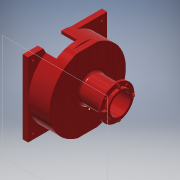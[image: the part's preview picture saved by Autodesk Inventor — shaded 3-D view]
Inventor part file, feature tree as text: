
AUTODESK INVENTOR PART (.ipt)
format: ipt  version: 2019 (Build 230136000, 136)  size: 973,824 bytes
history: native  units: mm
features: sketch x42, extrude x40, projected_geometry x19, other x6, fillet x6, reference x2
ambient origin geometry x8: Origin, YZ Plane, XZ Plane, XY Plane, X Axis, Y Axis, Z Axis, Center Point
bodies: Body1 (feature_tree), Body2 (feature_tree)
feature tree (115):
  other  "Твердое тело1"
  other  "0ae4c1a17e304db4a8c8e39318f74883.stl"
  extrude  "Выдавливание1"  Depth=3.0mm TaperAngle=0.0deg
  extrude  "Выдавливание2"  Depth=43.0mm
  extrude  "Выдавливание3"  Depth=25.0mm TaperAngle=0.0deg
  extrude  "Выдавливание4"  Depth=20.0mm
  extrude  "Выдавливание5"  Depth=20.0mm
  extrude  "Выдавливание6"  Depth=50.0mm TaperAngle=0.0deg
  extrude  "Выдавливание7"  Depth=34.0mm
  extrude  "Выдавливание8"  Depth=2.0mm
  extrude  "Выдавливание9"  Depth=2.0mm
  extrude  "Выдавливание10"  Depth=1.0mm TaperAngle=0.0deg
  sketch  "Эскиз15"
  sketch  "Эскиз16"
  extrude  "Выдавливание11"  Depth=25.0mm TaperAngle=0.0deg
  extrude  "Выдавливание12"  Depth=4.0mm
  extrude  "Выдавливание13"  Depth=4.0mm
  extrude  "Выдавливание14"  Depth=4.0mm
  extrude  "Выдавливание15"  Depth=4.0mm
  extrude  "Выдавливание16"  Depth=4.5mm
  fillet  "Сопряжение1"  Radius=4.5mm
  fillet  "Сопряжение2"  Radius=4.5mm
  extrude  "Выдавливание17"  Depth=4.5mm
  extrude  "Выдавливание18"  Depth=25.0mm TaperAngle=0.0deg
  extrude  "Выдавливание19"  Depth=7.2mm
  extrude  "Выдавливание20"  Depth=7.2mm
  extrude  "Выдавливание21"  Depth=7.2mm
  extrude  "Выдавливание22"  Depth=7.2mm
  fillet  "Сопряжение3"  Radius=2.0mm
  extrude  "Выдавливание23"  Depth=15.0mm TaperAngle=0.0deg
  extrude  "Выдавливание24"  Depth=15.0mm
  extrude  "Выдавливание25"  Depth=3.0mm
  extrude  "Выдавливание26"  Depth=13.663525mm
  extrude  "Выдавливание27"  Depth=30.32705mm
  extrude  "Выдавливание28"  Depth=8.5mm TaperAngle=0.0deg
  fillet  "Сопряжение4"  Radius=8.5mm
  extrude  "Выдавливание29"  Depth=38.8mm
  extrude  "Выдавливание30"  Depth=22.0mm TaperAngle=0.0deg
  extrude  "Выдавливание31"  Depth=25.0mm TaperAngle=0.0deg
  extrude  "Выдавливание32"  Depth=10.0mm TaperAngle=0.0deg
  fillet  "Сопряжение5"  Radius=3.5mm
  sketch  "Эскиз38"
  extrude  "Выдавливание33"  Depth=3.5mm TaperAngle=0.0deg
  extrude  "Выдавливание34"  Depth=1.0mm TaperAngle=0.0deg
  extrude  "Выдавливание35"  Depth=2.0mm
  fillet  "Сопряжение6"  Radius=2.0mm
  extrude  "Выдавливание37"  Depth=10.0mm TaperAngle=0.0deg
  extrude  "Выдавливание38"  Depth=3.0mm TaperAngle=0.0deg
  extrude  "Выдавливание39"  Depth=3.0mm TaperAngle=0.0deg
  extrude  "Выдавливание40"  Depth=28.0mm
  extrude  "Выдавливание41"  TaperAngle=135.0deg  [1 undecoded]
  sketch  "Эскиз2"
  sketch  "Эскиз3"
  sketch  "Эскиз5"
  sketch  "Эскиз6"
  projected_geometry  "Спроецированная петля1"
  sketch  "Эскиз8"
  sketch  "Эскиз9"
  projected_geometry  "Спроецированная петля3"
  sketch  "Эскиз11"
  sketch  "Эскиз12"
  projected_geometry  "Спроецированная петля4"
  sketch  "Эскиз13"
  sketch  "Эскиз14"
  sketch  "Эскиз17"
  sketch  "Эскиз18"
  projected_geometry  "Спроецированная петля5"
  sketch  "Эскиз19"
  projected_geometry  "Спроецированная петля6"
  projected_geometry  "Спроецированная петля7"
  sketch  "Эскиз20"
  projected_geometry  "Спроецированная петля8"
  sketch  "Эскиз21"
  projected_geometry  "Спроецированная петля9"
  sketch  "Эскиз22"
  projected_geometry  "Спроецированная петля10"
  sketch  "Эскиз23"
  sketch  "Эскиз24"
  sketch  "Эскиз25"
  sketch  "Эскиз26"
  sketch  "Эскиз27"
  sketch  "Эскиз28"
  sketch  "Эскиз29"
  sketch  "Эскиз30"
  sketch  "Эскиз31"
  projected_geometry  "Спроецированная петля11"
  sketch  "Эскиз32"
  projected_geometry  "Спроецированная петля12"
  sketch  "Эскиз33"
  sketch  "Эскиз34"
  sketch  "Эскиз35"
  projected_geometry  "Спроецированная петля13"
  sketch  "Эскиз36"
  sketch  "Эскиз37"
  sketch  "Эскиз39"
  projected_geometry  "Спроецированная петля14"
  sketch  "Эскиз40"
  projected_geometry  "Спроецированная петля15"
  sketch  "Эскиз41"
  sketch  "Эскиз43"
  projected_geometry  "Спроецированная петля17"
  sketch  "Эскиз44"
  reference  "Ссылка1"
  sketch  "Эскиз45"
  projected_geometry  "Спроецированная петля18"
  projected_geometry  "Спроецированная петля19"
  sketch  "Эскиз46"
  projected_geometry  "Спроецированная петля20"
  projected_geometry  "Спроецированная петля21"
  sketch  "Эскиз47"
  reference  "Ссылка2"
  other  "ЭлементСетки1"
  parser-record x1  (decoder bookkeeping rows leaked as tree rows — omitted from the tree; the rows remain in map.json)
  other  "kowsh.iam"
  other  "Барабан:1"
note: 1 required parameter value undecoded (feature->parameter linkage not recoverable at this tier; creation-order binding heuristic only, values carry confidence <= 0.55)
note: 1 file-system path scrubbed to <path> (originals preserved in map.json)
